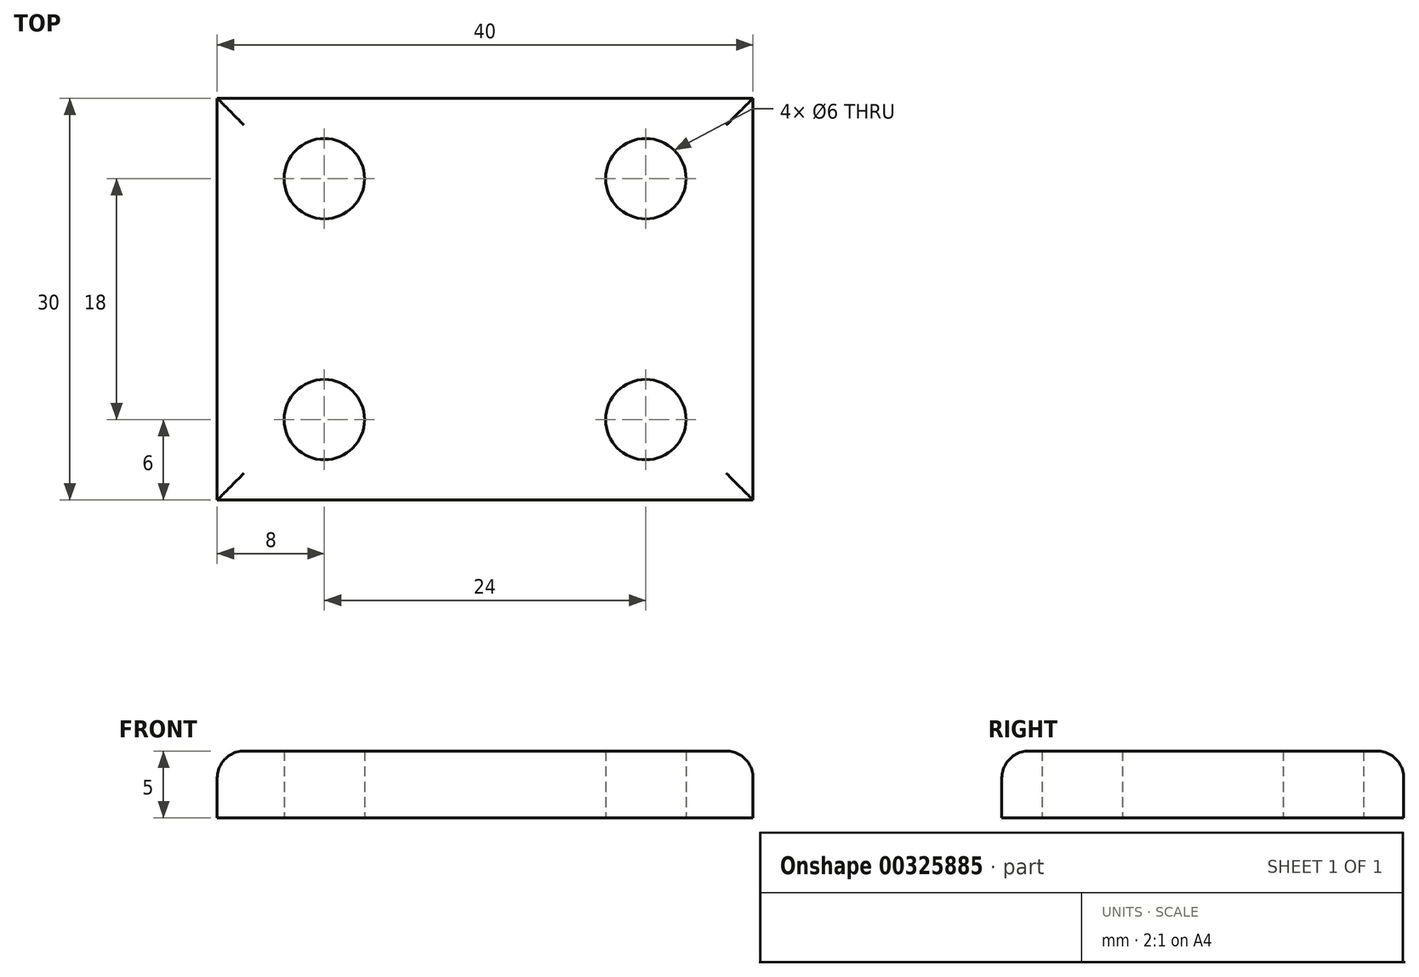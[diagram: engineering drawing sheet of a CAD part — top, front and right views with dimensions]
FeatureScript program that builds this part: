
annotation { "Feature Type Name" : "Feature", "Feature Type Description" : "" }
export const myFeature = defineFeature(function(context is Context, id is Id, definition is map)
    precondition{}
    {
        {
            var Q0;
            Q0=qCreatedBy(makeId("Top.planeOp"),FACE);
            var sketch = newSketch(context, id + "F0", { "sketchPlane" : qUnion([Q0])});
            skCircle(sketch, "E0", {"center": v(-12, 9) * mm, "radius": 3 * mm});
            skSolve(sketch);
        }
        {
            var Q0;
            Q0 = qSketchRegion(id + "F0", true);
            extrude(context, id + "F1", {"entities" : qUnion([Q0]), "depth" : 25 * mm});
        }
        {
            var Q0;
            Q0=makeQuery(id+"F1.opExtrude","SWEPT_BODY",BODY,{"disambiguationData":[OSD([sQuery(id+"F0.wireOp",EDGE,"E0")])]});
            var Q1;
            Q1=qCreatedBy(makeId("Right.planeOp"),FACE);
            mirror(context, id + "F2", {"entities" : qUnion([Q0]), "mirrorPlane" : qUnion([Q1])});
        }
        {
            var Q0;
            Q0=makeQuery(id+"F1.opExtrude","SWEPT_BODY",BODY,{"disambiguationData":[OSD([sQuery(id+"F0.wireOp",EDGE,"E0")])]});
            var Q1;
            Q1=makeQuery(id+"F2.opPattern","COPY",BODY,{"derivedFrom":makeQuery(id+"F1.opExtrude","SWEPT_BODY",BODY,{"disambiguationData":[OSD([sQuery(id+"F0.wireOp",EDGE,"E0")])]}),"instanceName":"1"});
            var Q2;
            Q2=qCreatedBy(makeId("Front.planeOp"),FACE);
            mirror(context, id + "F3", {"entities" : qUnion([Q0, Q1]), "mirrorPlane" : qUnion([Q2])});
        }
        {
            var Q0;
            Q0=qCreatedBy(makeId("Top.planeOp"),FACE);
            var sketch = newSketch(context, id + "F4", { "sketchPlane" : qUnion([Q0])});
            skLineSegment(sketch, "E1.bottom", {"start": v(-20, 15) * mm, "end": v(20, 15) * mm});
            skLineSegment(sketch, "E1.top", {"start": v(-20, -15) * mm, "end": v(20, -15) * mm});
            skLineSegment(sketch, "E1.left", {"start": v(-20, 15) * mm, "end": v(-20, -15) * mm});
            skLineSegment(sketch, "E1.right", {"start": v(20, 15) * mm, "end": v(20, -15) * mm});
            skSolve(sketch);
        }
        {
            var Q0;
            Q0 = qSketchRegion(id + "F4", true);
            extrude(context, id + "F5", {"entities" : qUnion([Q0]), "depth" : 5 * mm});
        }
        {
            var Q0;
            Q0=makeQuery(id+"F1.opExtrude","SWEPT_BODY",BODY,{"disambiguationData":[OSD([sQuery(id+"F0.wireOp",EDGE,"E0")])]});
            var Q1;
            Q1=makeQuery(id+"F2.opPattern","COPY",BODY,{"derivedFrom":makeQuery(id+"F1.opExtrude","SWEPT_BODY",BODY,{"disambiguationData":[OSD([sQuery(id+"F0.wireOp",EDGE,"E0")])]}),"instanceName":"1"});
            var Q2;
            Q2=makeQuery(id+"F3.opPattern","COPY",BODY,{"derivedFrom":makeQuery(id+"F1.opExtrude","SWEPT_BODY",BODY,{"disambiguationData":[OSD([sQuery(id+"F0.wireOp",EDGE,"E0")])]}),"instanceName":"1"});
            var Q3;
            Q3=makeQuery(id+"F3.opPattern","COPY",BODY,{"derivedFrom":makeQuery(id+"F2.opPattern","COPY",BODY,{"derivedFrom":makeQuery(id+"F1.opExtrude","SWEPT_BODY",BODY,{"disambiguationData":[OSD([sQuery(id+"F0.wireOp",EDGE,"E0")])]}),"instanceName":"1"}),"instanceName":"1"});
            var Q4;
            Q4=makeQuery(id+"F5.opExtrude","SWEPT_BODY",BODY,{"disambiguationData":[OSD([sQuery(id+"F4.wireOp",EDGE,"E1.bottom"),sQuery(id+"F4.wireOp",EDGE,"E1.top"),sQuery(id+"F4.wireOp",EDGE,"E1.left"),sQuery(id+"F4.wireOp",EDGE,"E1.right")])]});
            booleanBodies(context, id + "F6", {"operationType" : BooleanOperationType.SUBTRACTION, "tools" : qUnion([Q0, Q1, Q2, Q3]), "targets" : qUnion([Q4])});
        }
        {
            var Q0;
            Q0=makeQuery(id+"F5.opExtrude","CAP_EDGE",EDGE,{"disambiguationData":[OSD([sQuery(id+"F4.wireOp",EDGE,"E1.top")])],"isStart":false});
            var Q1;
            Q1=makeQuery(id+"F5.opExtrude","CAP_EDGE",EDGE,{"disambiguationData":[OSD([sQuery(id+"F4.wireOp",EDGE,"E1.left")])],"isStart":false});
            var Q2;
            Q2=makeQuery(id+"F5.opExtrude","CAP_EDGE",EDGE,{"disambiguationData":[OSD([sQuery(id+"F4.wireOp",EDGE,"E1.bottom")])],"isStart":false});
            var Q3;
            Q3=makeQuery(id+"F5.opExtrude","CAP_EDGE",EDGE,{"disambiguationData":[OSD([sQuery(id+"F4.wireOp",EDGE,"E1.right")])],"isStart":false});
            fillet(context, id + "F7", {"entities" : qUnion([Q0, Q1, Q2, Q3]), "radius" : 2 * mm, "tangentPropagation" : true, "allowEdgeOverflow" : false});
        }
    });
